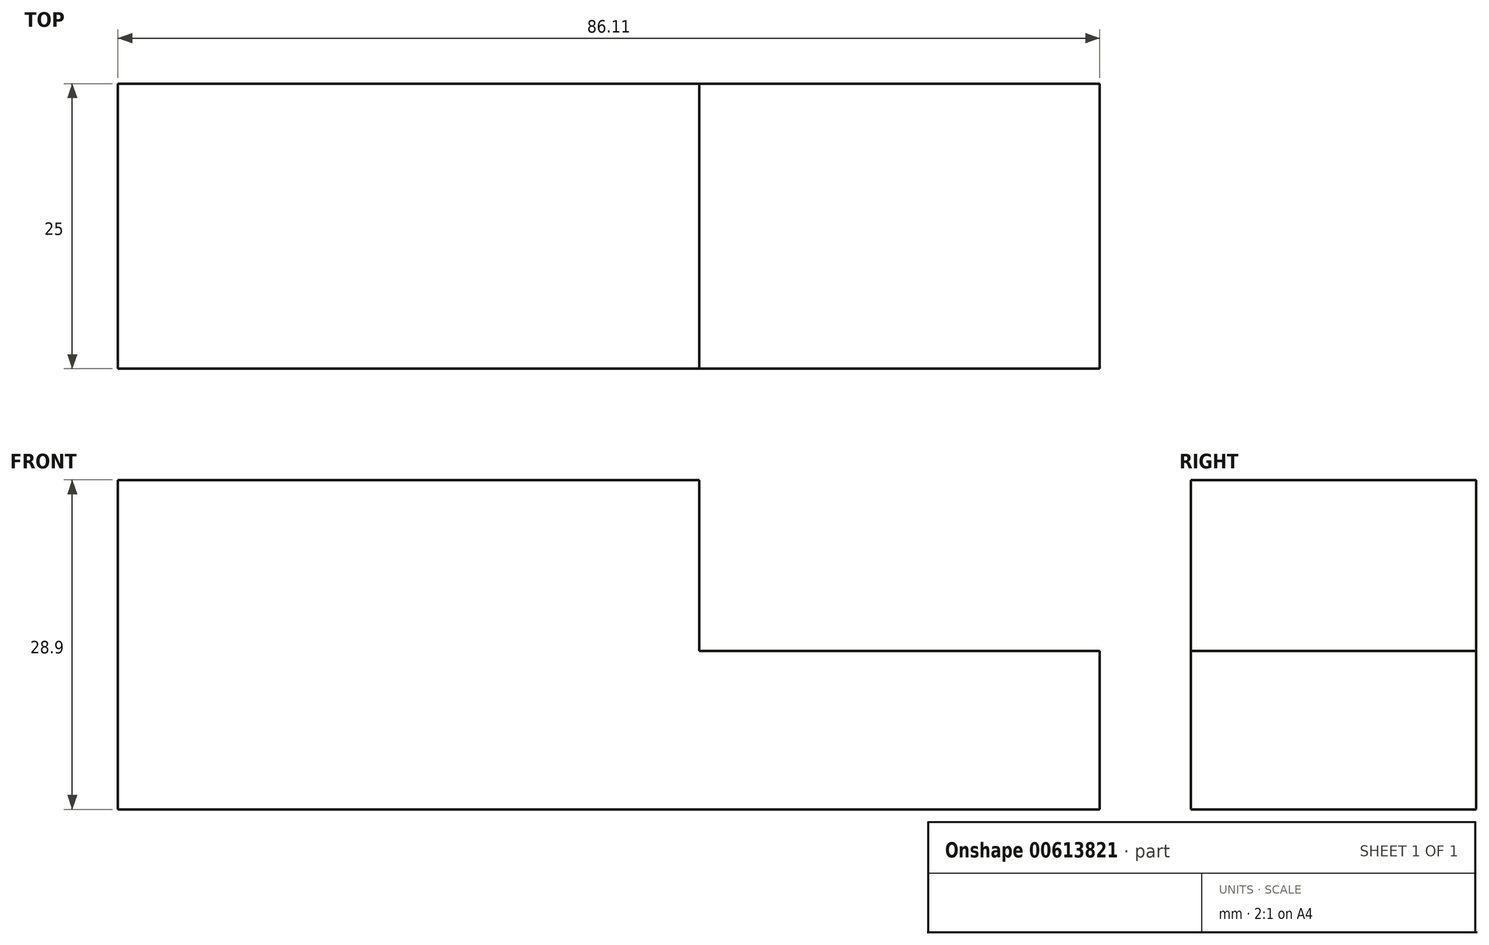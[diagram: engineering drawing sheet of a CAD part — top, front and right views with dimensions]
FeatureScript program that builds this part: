
annotation { "Feature Type Name" : "Feature", "Feature Type Description" : "" }
export const myFeature = defineFeature(function(context is Context, id is Id, definition is map)
    precondition{}
    {
        {
            var Q0;
            Q0=qCreatedBy(makeId("Front.planeOp"),FACE);
            var sketch = newSketch(context, id + "F0", { "sketchPlane" : qUnion([Q0])});
            skLineSegment(sketch, "E0", {"start": v(-67.84, 42.92) * mm, "end": v(-16.85, 42.92) * mm});
            skLineSegment(sketch, "E1", {"start": v(-16.85, 42.92) * mm, "end": v(-16.85, 27.9) * mm});
            skLineSegment(sketch, "E2", {"start": v(-16.85, 27.9) * mm, "end": v(18.27, 27.9) * mm});
            skLineSegment(sketch, "E3", {"start": v(18.27, 27.9) * mm, "end": v(18.27, 14.02) * mm});
            skLineSegment(sketch, "E4", {"start": v(18.27, 14.02) * mm, "end": v(-67.84, 14.02) * mm});
            skLineSegment(sketch, "E5", {"start": v(-67.84, 14.02) * mm, "end": v(-67.84, 42.92) * mm});
            skSolve(sketch);
        }
        {
            var Q0;
            Q0 = qSketchRegion(id + "F0", true);
            extrude(context, id + "F1", {"entities" : qUnion([Q0]), "depth" : 25 * mm, "offsetDistance" : 25 * mm});
        }
    });
